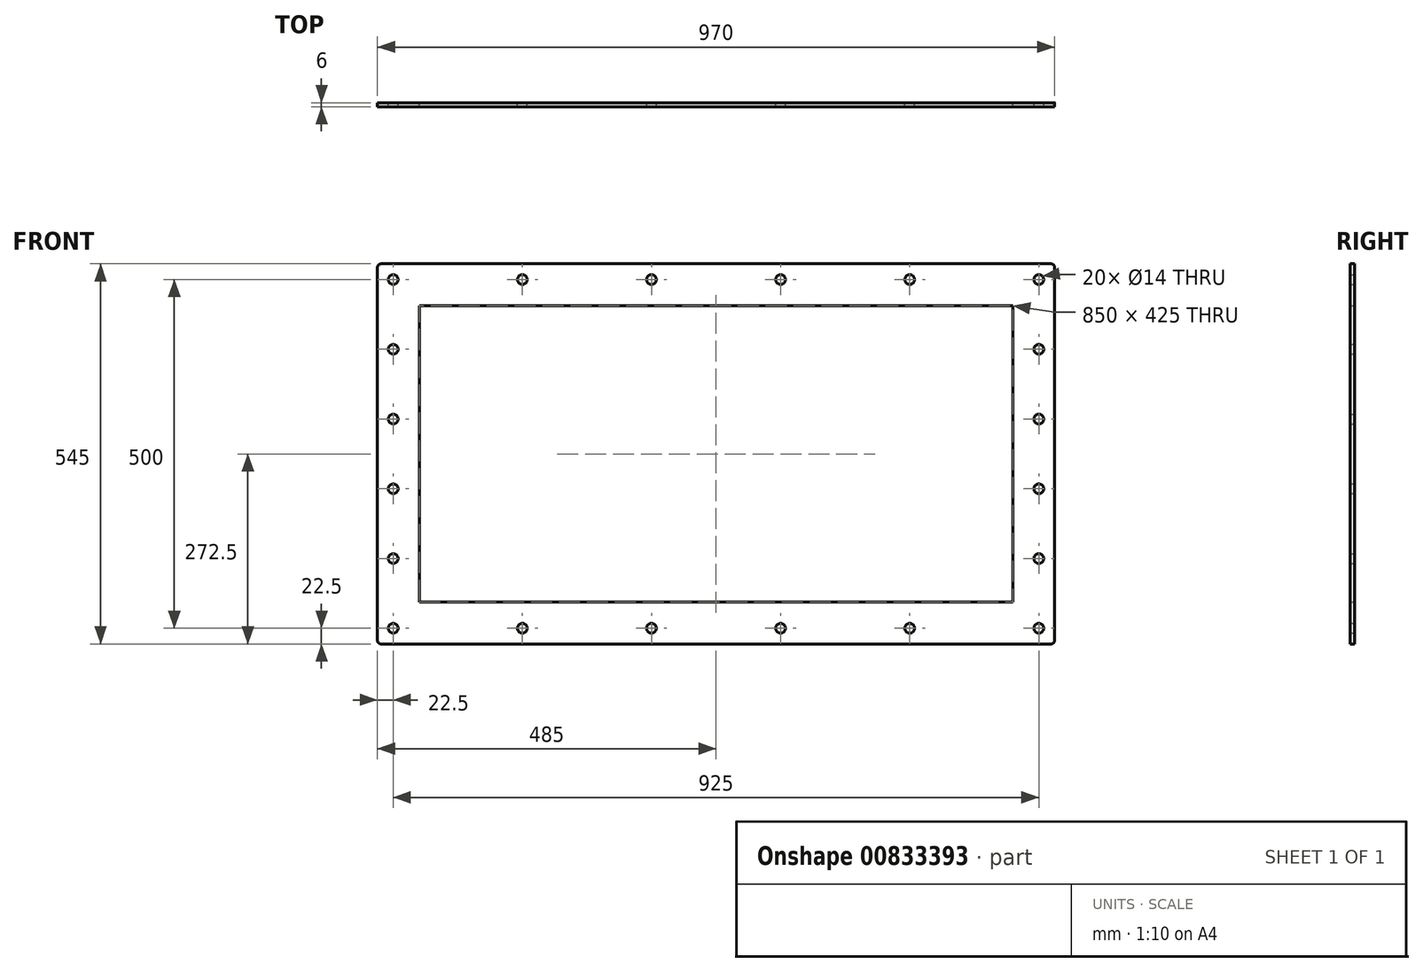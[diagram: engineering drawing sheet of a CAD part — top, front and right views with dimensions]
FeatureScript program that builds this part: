
annotation { "Feature Type Name" : "Feature", "Feature Type Description" : "" }
export const myFeature = defineFeature(function(context is Context, id is Id, definition is map)
    precondition{}
    {
        {
            var Q0;
            Q0=qCreatedBy(makeId("Front.planeOp"),FACE);
            var sketch = newSketch(context, id + "F0", { "sketchPlane" : qUnion([Q0])});
            skLineSegment(sketch, "E0.bottom", {"start": v(425, -212.5) * mm, "end": v(-425, -212.5) * mm});
            skLineSegment(sketch, "E0.top", {"start": v(425, 212.5) * mm, "end": v(-425, 212.5) * mm});
            skLineSegment(sketch, "E0.left", {"start": v(425, -212.5) * mm, "end": v(425, 212.5) * mm});
            skLineSegment(sketch, "E0.right", {"start": v(-425, -212.5) * mm, "end": v(-425, 212.5) * mm});
            skPoint(sketch, "E0.middle", {"position": v(0, 0) * mm});
            skLineSegment(sketch, "E1.bottom", {"start": v(485, -272.5) * mm, "end": v(-485, -272.5) * mm});
            skLineSegment(sketch, "E1.top", {"start": v(485, 272.5) * mm, "end": v(-485, 272.5) * mm});
            skLineSegment(sketch, "E1.left", {"start": v(485, -272.5) * mm, "end": v(485, 272.5) * mm});
            skLineSegment(sketch, "E1.right", {"start": v(-485, -272.5) * mm, "end": v(-485, 272.5) * mm});
            skSolve(sketch);
        }
        {
            var Q0;
            Q0 = qSketchRegion(id + "F0", true);
            extrude(context, id + "F1", {"entities" : qUnion([Q0]), "depth" : 6 * mm, "offsetDistance" : 25 * mm});
        }
        {
            var Q0;
            Q0=makeQuery(id+"F1.opExtrude","SWEPT_EDGE",EDGE,{"disambiguationData":[OSD([sQuery(id+"F0.wireOp",EDGE,"E1.top"),sQuery(id+"F0.wireOp",EDGE,"E1.right")])]});
            var Q1;
            Q1=makeQuery(id+"F1.opExtrude","SWEPT_EDGE",EDGE,{"disambiguationData":[OSD([sQuery(id+"F0.wireOp",EDGE,"E1.top"),sQuery(id+"F0.wireOp",EDGE,"E1.left")])]});
            var Q2;
            Q2=makeQuery(id+"F1.opExtrude","SWEPT_EDGE",EDGE,{"disambiguationData":[OSD([sQuery(id+"F0.wireOp",EDGE,"E1.bottom"),sQuery(id+"F0.wireOp",EDGE,"E1.left")])]});
            var Q3;
            Q3=makeQuery(id+"F1.opExtrude","SWEPT_EDGE",EDGE,{"disambiguationData":[OSD([sQuery(id+"F0.wireOp",EDGE,"E1.bottom"),sQuery(id+"F0.wireOp",EDGE,"E1.right")])]});
            fillet(context, id + "F2", {"entities" : qUnion([Q0, Q1, Q2, Q3]), "radius" : 5 * mm, "tangentPropagation" : true, "allowEdgeOverflow" : false});
        }
        {
            var Q0;
            Q0=qCreatedBy(makeId("Front.planeOp"),FACE);
            var sketch = newSketch(context, id + "F3", { "sketchPlane" : qUnion([Q0])});
            skLineSegment(sketch, "E2", {"start": v(0, 0) * mm, "end": v(629.87, 0) * mm, "construction": true});
            skLineSegment(sketch, "E3", {"start": v(0, 0) * mm, "end": v(0, 549.78) * mm, "construction": true});
            skPoint(sketch, "E4", {"position": v(-462.5, -250) * mm});
            skPoint(sketch, "E5.0.1.0", {"position": v(-462.5, 250) * mm});
            skPoint(sketch, "E5.0.2.0", {"position": v(-462.5, 750) * mm});
            skPoint(sketch, "E5.0.3.0", {"position": v(-462.5, 1250) * mm});
            skPoint(sketch, "E5.0.4.0", {"position": v(-462.5, 1750) * mm});
            skPoint(sketch, "E5.0.5.0", {"position": v(-462.5, 2250) * mm});
            skPoint(sketch, "E5.1.0.0", {"position": v(462.5, -250) * mm});
            skPoint(sketch, "E5.1.1.0", {"position": v(462.5, 250) * mm});
            skPoint(sketch, "E5.1.2.0", {"position": v(462.5, 750) * mm});
            skPoint(sketch, "E5.1.3.0", {"position": v(462.5, 1250) * mm});
            skPoint(sketch, "E5.1.4.0", {"position": v(462.5, 1750) * mm});
            skPoint(sketch, "E5.1.5.0", {"position": v(462.5, 2250) * mm});
            skLineSegment(sketch, "E5.direction1", {"start": v(-462.5, -250) * mm, "end": v(462.5, -250) * mm, "construction": true});
            skLineSegment(sketch, "E5.direction2", {"start": v(-462.5, -250) * mm, "end": v(-462.5, 250) * mm, "construction": true});
            skPoint(sketch, "E6.1.0.0", {"position": v(-277.5, -250) * mm});
            skPoint(sketch, "E6.1.0.1", {"position": v(-277.5, 2250) * mm});
            skPoint(sketch, "E6.1.0.2", {"position": v(-277.5, 250) * mm});
            skPoint(sketch, "E6.2.0.0", {"position": v(-92.5, -250) * mm});
            skPoint(sketch, "E6.2.0.1", {"position": v(-92.5, 2250) * mm});
            skPoint(sketch, "E6.2.0.2", {"position": v(-92.5, 250) * mm});
            skPoint(sketch, "E6.3.0.0", {"position": v(92.5, -250) * mm});
            skPoint(sketch, "E6.3.0.1", {"position": v(92.5, 2250) * mm});
            skPoint(sketch, "E6.3.0.2", {"position": v(92.5, 250) * mm});
            skPoint(sketch, "E6.4.0.0", {"position": v(277.5, -250) * mm});
            skPoint(sketch, "E6.4.0.1", {"position": v(277.5, 2250) * mm});
            skPoint(sketch, "E6.4.0.2", {"position": v(277.5, 250) * mm});
            skLineSegment(sketch, "E6.direction1", {"start": v(-462.5, -250) * mm, "end": v(-277.5, -250) * mm, "construction": true});
            skPoint(sketch, "E7.0.1.0", {"position": v(-462.5, -150) * mm});
            skPoint(sketch, "E7.0.2.0", {"position": v(-462.5, -50) * mm});
            skPoint(sketch, "E7.0.3.0", {"position": v(-462.5, 50) * mm});
            skPoint(sketch, "E7.0.4.0", {"position": v(-462.5, 150) * mm});
            skPoint(sketch, "E7.1.1.0", {"position": v(462.5, -150) * mm});
            skPoint(sketch, "E7.1.2.0", {"position": v(462.5, -50) * mm});
            skPoint(sketch, "E7.1.3.0", {"position": v(462.5, 50) * mm});
            skPoint(sketch, "E7.1.4.0", {"position": v(462.5, 150) * mm});
            skPoint(sketch, "E7.2.0.0", {"position": v(1387.5, -250) * mm});
            skPoint(sketch, "E7.2.1.0", {"position": v(1387.5, -150) * mm});
            skPoint(sketch, "E7.2.2.0", {"position": v(1387.5, -50) * mm});
            skPoint(sketch, "E7.2.3.0", {"position": v(1387.5, 50) * mm});
            skPoint(sketch, "E7.2.4.0", {"position": v(1387.5, 150) * mm});
            skLineSegment(sketch, "E7.direction2", {"start": v(-462.5, -250) * mm, "end": v(-462.5, -150) * mm, "construction": true});
            skSolve(sketch);
        }
        {
            var Q0;
            Q0=sQuery(id+"F3.wireOp",VERTEX,"E5.1.1.0");
            var Q1;
            Q1=sQuery(id+"F3.wireOp",VERTEX,"E6.4.0.2");
            var Q2;
            Q2=sQuery(id+"F3.wireOp",VERTEX,"E6.3.0.2");
            var Q3;
            Q3=sQuery(id+"F3.wireOp",VERTEX,"E6.2.0.2");
            var Q4;
            Q4=sQuery(id+"F3.wireOp",VERTEX,"E5.0.1.0");
            var Q5;
            Q5=sQuery(id+"F3.wireOp",VERTEX,"E7.0.4.0");
            var Q6;
            Q6=sQuery(id+"F3.wireOp",VERTEX,"E7.0.3.0");
            var Q7;
            Q7=sQuery(id+"F3.wireOp",VERTEX,"E7.0.2.0");
            var Q8;
            Q8=sQuery(id+"F3.wireOp",VERTEX,"E7.0.1.0");
            var Q9;
            Q9=sQuery(id+"F3.wireOp",VERTEX,"E4");
            var Q10;
            Q10=sQuery(id+"F3.wireOp",VERTEX,"E6.1.0.0");
            var Q11;
            Q11=sQuery(id+"F3.wireOp",VERTEX,"E6.2.0.0");
            var Q12;
            Q12=sQuery(id+"F3.wireOp",VERTEX,"E6.3.0.0");
            var Q13;
            Q13=sQuery(id+"F3.wireOp",VERTEX,"E6.4.0.0");
            var Q14;
            Q14=sQuery(id+"F3.wireOp",VERTEX,"E5.1.0.0");
            var Q15;
            Q15=sQuery(id+"F3.wireOp",VERTEX,"E7.1.1.0");
            var Q16;
            Q16=sQuery(id+"F3.wireOp",VERTEX,"E7.1.2.0");
            var Q17;
            Q17=sQuery(id+"F3.wireOp",VERTEX,"E7.1.3.0");
            var Q18;
            Q18=sQuery(id+"F3.wireOp",VERTEX,"E7.1.4.0");
            var Q19;
            Q19=sQuery(id+"F3.wireOp",VERTEX,"E6.1.0.2");
            var Q20;
            Q20=makeQuery(id+"F1.opExtrude","SWEPT_BODY",BODY,{"disambiguationData":[OSD([sQuery(id+"F0.wireOp",EDGE,"E0.bottom"),sQuery(id+"F0.wireOp",EDGE,"E0.top"),sQuery(id+"F0.wireOp",EDGE,"E0.left"),sQuery(id+"F0.wireOp",EDGE,"E0.right"),sQuery(id+"F0.wireOp",EDGE,"E1.bottom"),sQuery(id+"F0.wireOp",EDGE,"E1.top"),sQuery(id+"F0.wireOp",EDGE,"E1.left"),sQuery(id+"F0.wireOp",EDGE,"E1.right")])]});
            hole(context, id + "F4", {"style" : HoleStyle.SIMPLE, "endStyle" : HoleEndStyle.THROUGH, "oppositeDirection" : true, "standardTappedOrClearance" : lookupTablePath({ "standard" : "ISO", "size" : "14", "type" : "Drilled" }), "standardBlindInLast" : lookupTablePath({ "standard" : "ISO", "size" : "14", "type" : "Drilled" }), "holeDiameter" : 14 * mm, "majorDiameter" : 5 * mm, "isTappedThrough" : true, "tappedDepth" : 12 * mm, "tapClearance" : 3, "locations" : qUnion([Q0, Q1, Q2, Q3, Q4, Q5, Q6, Q7, Q8, Q9, Q10, Q11, Q12, Q13, Q14, Q15, Q16, Q17, Q18, Q19]), "scope" : qUnion([Q20])});
        }
    });
